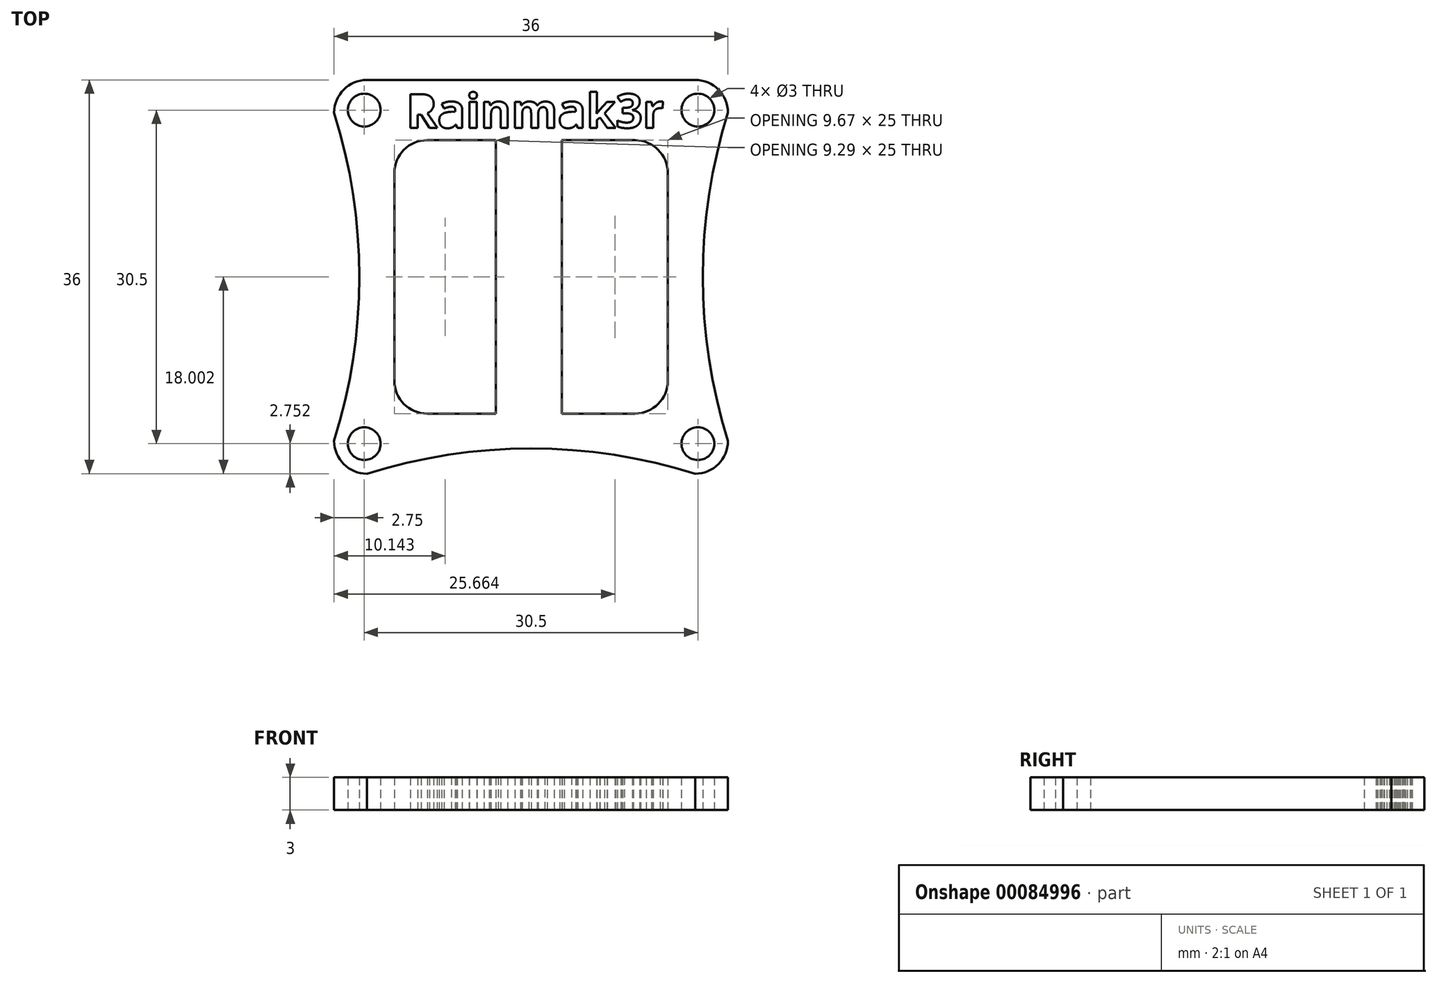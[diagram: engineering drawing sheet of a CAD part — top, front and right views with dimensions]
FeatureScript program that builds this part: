
annotation { "Feature Type Name" : "Feature", "Feature Type Description" : "" }
export const myFeature = defineFeature(function(context is Context, id is Id, definition is map)
    precondition{}
    {
        {
            var Q0;
            Q0=qCreatedBy(makeId("Top.planeOp"),FACE);
            var sketch = newSketch(context, id + "F0", { "sketchPlane" : qUnion([Q0])});
            skLineSegment(sketch, "E0.bottom", {"start": v(-33, 28.92) * mm, "end": v(-3, 28.92) * mm});
            skCircle(sketch, "E1", {"center": v(-33.25, 26.17) * mm, "radius": 1.5 * mm});
            skCircle(sketch, "E2", {"center": v(-2.75, 26.17) * mm, "radius": 1.5 * mm});
            skCircle(sketch, "E3", {"center": v(-33.25, -4.33) * mm, "radius": 1.5 * mm});
            skCircle(sketch, "E4", {"center": v(-2.75, -4.33) * mm, "radius": 1.5 * mm});
            skLineSegment(sketch, "E5.bottom", {"start": v(-27.5, 23.42) * mm, "end": v(-8.5, 23.42) * mm});
            skLineSegment(sketch, "E5.top", {"start": v(-27.5, -1.58) * mm, "end": v(-8.5, -1.58) * mm});
            skLineSegment(sketch, "E5.left", {"start": v(-30.5, 20.42) * mm, "end": v(-30.5, 1.42) * mm});
            skLineSegment(sketch, "E5.right", {"start": v(-5.5, 20.42) * mm, "end": v(-5.5, 1.42) * mm});
            skPoint(sketch, "E6.visualSharp", {"position": v(-36, 28.92) * mm});
            skArc(sketch, "E6.filletArc", {"start": v(-33, 28.92) * mm, "mid": v(-35.12, 28.04) * mm, "end": v(-36, 25.92) * mm});
            skPoint(sketch, "E7.visualSharp", {"position": v(0, 28.92) * mm});
            skArc(sketch, "E7.filletArc", {"start": v(0, 25.92) * mm, "mid": v(-0.88, 28.04) * mm, "end": v(-3, 28.92) * mm});
            skPoint(sketch, "E8.visualSharp", {"position": v(0, -7.08) * mm});
            skArc(sketch, "E8.filletArc", {"start": v(-3, -7.08) * mm, "mid": v(-0.88, -6.2) * mm, "end": v(0, -4.08) * mm});
            skPoint(sketch, "E9.visualSharp", {"position": v(-36, -7.08) * mm});
            skArc(sketch, "E9.filletArc", {"start": v(-36, -4.08) * mm, "mid": v(-35.12, -6.2) * mm, "end": v(-33, -7.08) * mm});
            skPoint(sketch, "E10.visualSharp", {"position": v(-30.5, 23.42) * mm});
            skArc(sketch, "E10.filletArc", {"start": v(-27.5, 23.42) * mm, "mid": v(-29.62, 22.54) * mm, "end": v(-30.5, 20.42) * mm});
            skPoint(sketch, "E11.visualSharp", {"position": v(-30.5, -1.58) * mm});
            skArc(sketch, "E11.filletArc", {"start": v(-30.5, 1.42) * mm, "mid": v(-29.62, -0.7) * mm, "end": v(-27.5, -1.58) * mm});
            skPoint(sketch, "E12.visualSharp", {"position": v(-5.5, 23.42) * mm});
            skArc(sketch, "E12.filletArc", {"start": v(-5.5, 20.42) * mm, "mid": v(-6.38, 22.54) * mm, "end": v(-8.5, 23.42) * mm});
            skPoint(sketch, "E13.visualSharp", {"position": v(-5.5, -1.58) * mm});
            skArc(sketch, "E13.filletArc", {"start": v(-8.5, -1.58) * mm, "mid": v(-6.38, -0.7) * mm, "end": v(-5.5, 1.42) * mm});
            skLineSegment(sketch, "E14", {"start": v(-21.21, 23.42) * mm, "end": v(-21.21, -1.58) * mm});
            skLineSegment(sketch, "E15", {"start": v(-15.17, 23.42) * mm, "end": v(-15.17, -1.58) * mm});
            skText(sketch, "E16", { "text": "Rainmak3r", "fontName": "OpenSans-Bold.ttf"});
            skArc(sketch, "E17", {"start": v(-3, -7.08) * mm, "mid": v(-18, -4.77) * mm, "end": v(-33, -7.08) * mm});
            skArc(sketch, "E18", {"start": v(-36, -4.08) * mm, "mid": v(-33.7, 10.92) * mm, "end": v(-36, 25.92) * mm});
            skArc(sketch, "E19", {"start": v(0, 25.92) * mm, "mid": v(-2.3, 10.92) * mm, "end": v(0, -4.08) * mm});
            const initialGuessF0  = {"E16": [-0.02942, 0.02455, 1, 0, 0.00311]};
            skSetInitialGuess(sketch, initialGuessF0);
            skSolve(sketch);
        }
        {
            var Q0;
            Q0=makeQuery(id+"F0.imprint","IMPRINT",FACE,{"disambiguationData":[TD([[makeQuery(id+"F0.imprint","IMPRINT",EDGE,{"derivedFrom":sQuery(id+"F0.wireOp",EDGE,"E0.bottom")}),-1.0]])]});
            var Q1;
            {var subQ0=sQuery(id+"F0.wireOp",EDGE,"E14");Q1=makeQuery(id+"F0.imprint","IMPRINT",FACE,{"disambiguationData":[TD([[makeQuery(id+"F0.imprint","IMPRINT",EDGE,{"derivedFrom":subQ0}),1.0]])]});}
            extrude(context, id + "F1", {"entities" : qUnion([Q0, Q1]), "depth" : 3 * mm});
        }
    });
